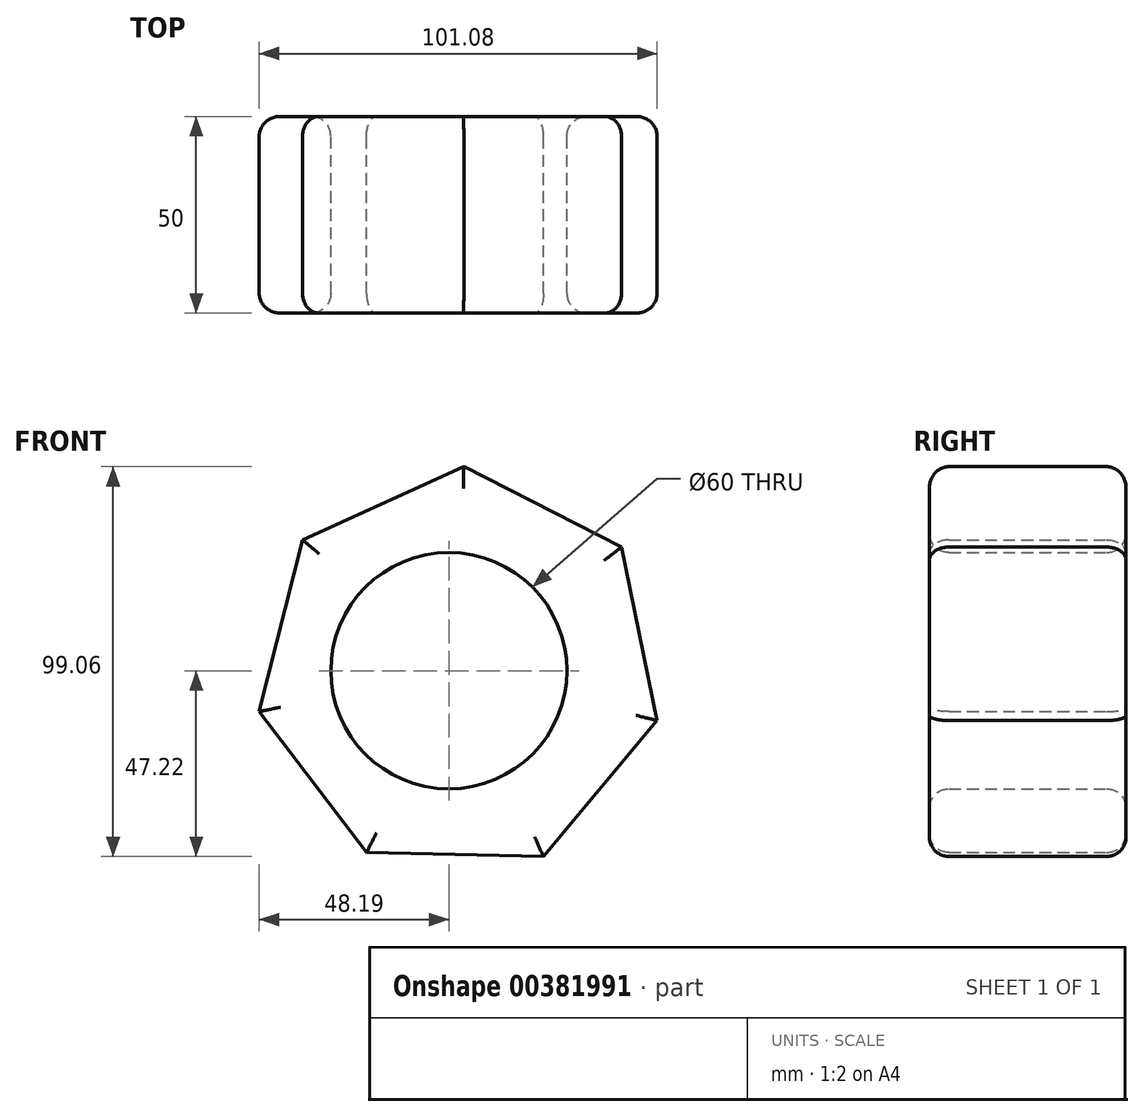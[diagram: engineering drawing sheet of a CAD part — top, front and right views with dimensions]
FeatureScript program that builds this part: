
annotation { "Feature Type Name" : "Feature", "Feature Type Description" : "" }
export const myFeature = defineFeature(function(context is Context, id is Id, definition is map)
    precondition{}
    {
        {
            var Q0;
            Q0=qCreatedBy(makeId("Front.planeOp"),FACE);
            var sketch = newSketch(context, id + "F0", { "sketchPlane" : qUnion([Q0])});
            skCircle(sketch, "E0.cCircle", {"center": v(2.61, 0) * mm, "radius": 46.72 * mm, "construction": true});
            skLineSegment(sketch, "E0.0", {"start": v(3.79, 51.84) * mm, "end": v(43.88, 31.4) * mm});
            skLineSegment(sketch, "E0.1", {"start": v(43.88, 31.4) * mm, "end": v(52.9, -12.68) * mm});
            skLineSegment(sketch, "E0.2", {"start": v(52.9, -12.68) * mm, "end": v(24.05, -47.22) * mm});
            skLineSegment(sketch, "E0.3", {"start": v(24.05, -47.22) * mm, "end": v(-20.94, -46.2) * mm});
            skLineSegment(sketch, "E0.4", {"start": v(-20.94, -46.2) * mm, "end": v(-48.2, -10.4) * mm});
            skLineSegment(sketch, "E0.5", {"start": v(-48.2, -10.4) * mm, "end": v(-37.19, 33.24) * mm});
            skLineSegment(sketch, "E0.6", {"start": v(-37.19, 33.24) * mm, "end": v(3.79, 51.84) * mm});
            skPoint(sketch, "E0.0.midPoint", {"position": v(23.83, 41.62) * mm});
            skSolve(sketch);
        }
        {
            var Q0;
            Q0=makeQuery(id+"F0.imprint","IMPRINT",FACE,{"disambiguationData":[TD([[makeQuery(id+"F0.imprint","IMPRINT",EDGE,{"derivedFrom":sQuery(id+"F0.wireOp",EDGE,"E0.0")}),-1.0]])]});
            extrude(context, id + "F1", {"entities" : qUnion([Q0]), "depth" : 50 * mm});
        }
        {
            var Q0;
            Q0=qCreatedBy(makeId("Front.planeOp"),FACE);
            var sketch = newSketch(context, id + "F2", { "sketchPlane" : qUnion([Q0])});
            skCircle(sketch, "E1", {"center": v(0, 0) * mm, "radius": 30 * mm});
            skSolve(sketch);
        }
        {
            var Q0;
            Q0 = qSketchRegion(id + "F2", true);
            extrude(context, id + "F3", {"entities" : qUnion([Q0]), "operationType" : NewBodyOperationType.REMOVE, "endBound" : BoundingType.THROUGH_ALL, "depth" : 55.6 * mm});
        }
        {
            var Q0;
            Q0=makeQuery(id+"F1.opExtrude","CAP_FACE",FACE,{"disambiguationData":[OSD([sQuery(id+"F0.wireOp",EDGE,"E0.0"),sQuery(id+"F0.wireOp",EDGE,"E0.1"),sQuery(id+"F0.wireOp",EDGE,"E0.2"),sQuery(id+"F0.wireOp",EDGE,"E0.3"),sQuery(id+"F0.wireOp",EDGE,"E0.4"),sQuery(id+"F0.wireOp",EDGE,"E0.5"),sQuery(id+"F0.wireOp",EDGE,"E0.6")])],"isStart":false});
            var Q1;
            Q1=makeQuery(id+"F1.opExtrude","CAP_FACE",FACE,{"disambiguationData":[OSD([sQuery(id+"F0.wireOp",EDGE,"E0.0"),sQuery(id+"F0.wireOp",EDGE,"E0.1"),sQuery(id+"F0.wireOp",EDGE,"E0.2"),sQuery(id+"F0.wireOp",EDGE,"E0.3"),sQuery(id+"F0.wireOp",EDGE,"E0.4"),sQuery(id+"F0.wireOp",EDGE,"E0.5"),sQuery(id+"F0.wireOp",EDGE,"E0.6")])],"isStart":true});
            fillet(context, id + "F4", {"entities" : qUnion([Q0, Q1]), "radius" : 5 * mm, "tangentPropagation" : true, "allowEdgeOverflow" : false});
        }
    });
